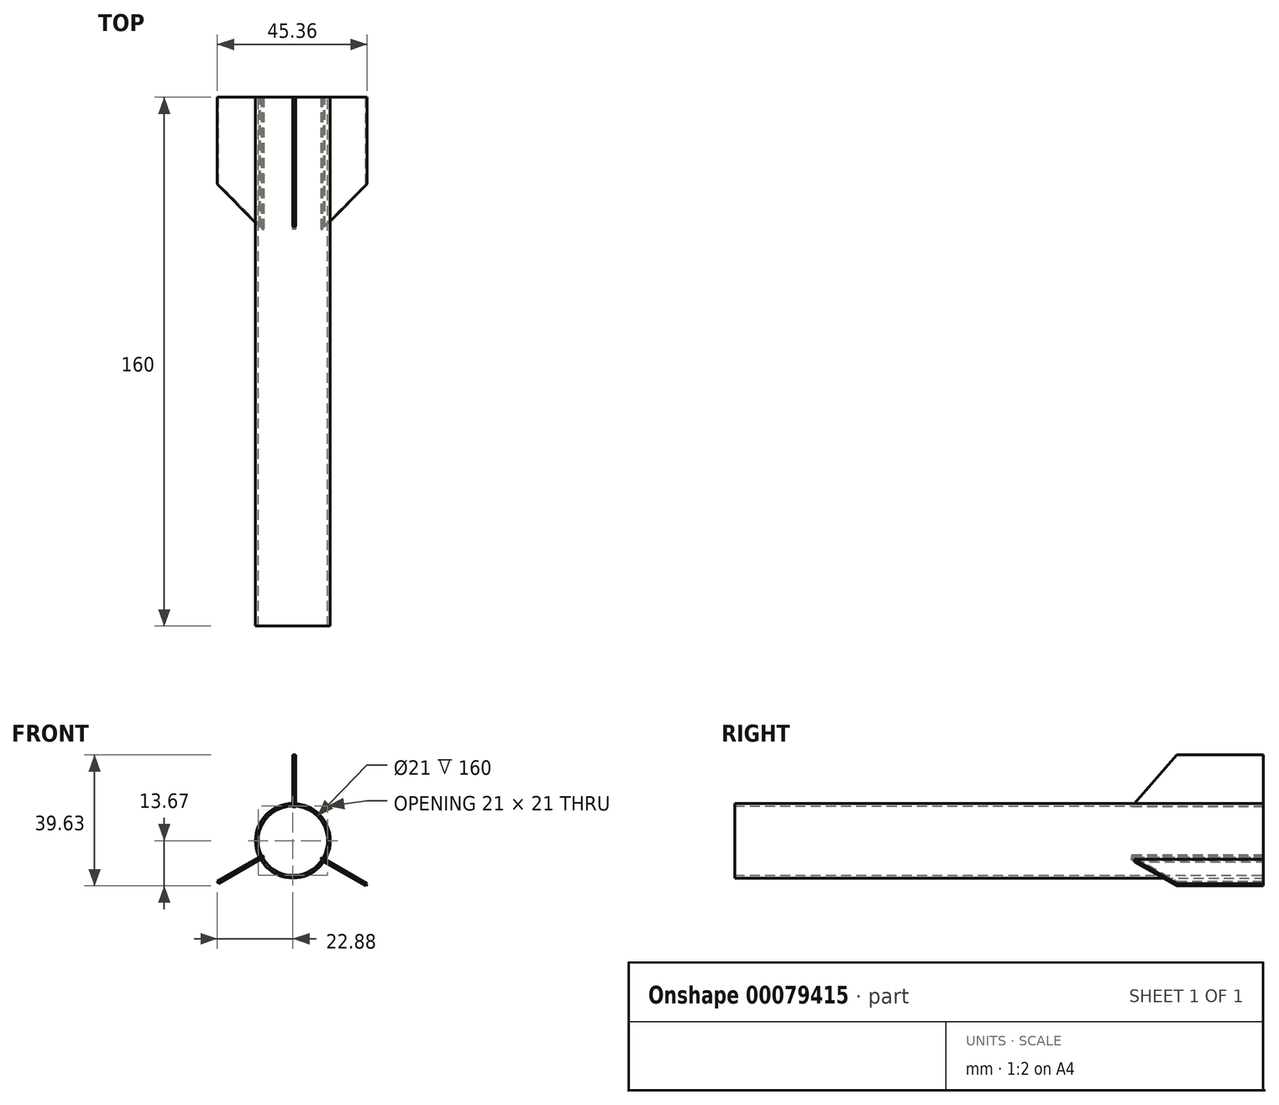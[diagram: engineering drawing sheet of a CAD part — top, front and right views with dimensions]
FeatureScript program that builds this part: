
annotation { "Feature Type Name" : "Feature", "Feature Type Description" : "" }
export const myFeature = defineFeature(function(context is Context, id is Id, definition is map)
    precondition{}
    {
        {
            var Q0;
            Q0=qCreatedBy(makeId("Front.planeOp"),FACE);
            var sketch = newSketch(context, id + "F0", { "sketchPlane" : qUnion([Q0])});
            skCircle(sketch, "E0", {"center": v(0, 0) * mm, "radius": 10.5 * mm});
            skCircle(sketch, "E1", {"center": v(0, 0) * mm, "radius": 11.3 * mm});
            skSolve(sketch);
        }
        {
            var Q0;
            Q0=makeQuery(id+"F0.imprint","IMPRINT",FACE,{"disambiguationData":[TD([[makeQuery(id+"F0.imprint","IMPRINT",EDGE,{"derivedFrom":sQuery(id+"F0.wireOp",EDGE,"E0")}),-1.0]])]});
            extrude(context, id + "F1", {"entities" : qUnion([Q0]), "depth" : 160 * mm});
        }
        {
            var Q0;
            Q0=qCreatedBy(makeId("Right.planeOp"),FACE);
            var sketch = newSketch(context, id + "F2", { "sketchPlane" : qUnion([Q0])});
            skLineSegment(sketch, "E2", {"start": v(0, 10.2) * mm, "end": v(-40, 10.2) * mm});
            skLineSegment(sketch, "E3", {"start": v(-40, 10.2) * mm, "end": v(-26.18, 25.96) * mm});
            skLineSegment(sketch, "E4", {"start": v(-26.18, 25.96) * mm, "end": v(0, 25.96) * mm});
            skLineSegment(sketch, "E5", {"start": v(0, 25.96) * mm, "end": v(0, 10.2) * mm});
            skSolve(sketch);
        }
        {
            var Q0;
            Q0=makeQuery(id+"F2.imprint","IMPRINT",FACE,{"disambiguationData":[TD([[makeQuery(id+"F2.imprint","IMPRINT",EDGE,{"derivedFrom":sQuery(id+"F2.wireOp",EDGE,"E2")}),-1.0]])]});
            extrude(context, id + "F3", {"entities" : qUnion([Q0]), "depth" : 0.8 * mm});
        }
        {
            var Q0;
            Q0=makeQuery(id+"F3.opExtrude","SWEPT_BODY",BODY,{"disambiguationData":[OSD([sQuery(id+"F2.wireOp",EDGE,"E2"),sQuery(id+"F2.wireOp",EDGE,"E3"),sQuery(id+"F2.wireOp",EDGE,"E4"),sQuery(id+"F2.wireOp",EDGE,"E5")])]});
            var Q1;
            Q1=makeQuery(id+"F1.opExtrude","SWEPT_FACE",FACE,{"disambiguationData":[OSD([sQuery(id+"F0.wireOp",EDGE,"E1")])]});
            circularPattern(context, id + "F4", {"operationType" : NewBodyOperationType.ADD, "entities" : qUnion([Q0]), "axis" : qUnion([Q1]), "angle" : 360 * degree, "instanceCount" : 3, "equalSpace" : true});
        }
    });
